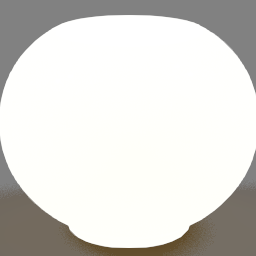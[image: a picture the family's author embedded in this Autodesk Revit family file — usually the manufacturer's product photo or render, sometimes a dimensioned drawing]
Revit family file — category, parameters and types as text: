
# Revit family: 3-020X-xx Avior Mirror
name_source: partatom
category: Lighting Fixtures
units: mm (PartAtom-declared; Revit-internal decimal feet)

## family parameters
Always vertical = Yes
Cut with Voids When Loaded = No
Host = Wall
Light Source = No
OmniClass Number = 23.80.70.00
OmniClass Title = Lighting
Part Type = Normal
Room Calculation Point = No
Round Connector Dimension = Use Diameter
Shared = No

## types (3) — shared parameters
Lamp = LED Array
Manufacturer = Vanita by Oxygen
Metal Finish 1 = 15 - Black
Model = 3-020X-xx / Avior Round
References = Ref. 3 = 120 V / Ref. 37 = 277 V
URL = www.oxygenlighting.com
Voltage = 120 V
Voltage Input = 120 V or 277 V - 50/60 Hz
zero-valued in all types: Default Elevation

## per-type parameters (varying)
| type | Diameter | Wattage Comments |
| 3-0201-15 / Black | 762 mm  [stored 2.5 ft] | 1 x 48 W at 120 V |
| 3-0202-15 / Black | 914 mm  [stored 2.99869 ft] | 1 x 50.7 W at 120 V |
| 3-0203-15 / Black | 1219 mm | 1 x 99.8 W at 120 V |

note: [stored X ft] marks values corroborated as IEEE doubles in the binary element streams (Revit-internal decimal feet)

## geometry (parser evidence)
native form markers: Sweep x5
no freeform markers — native parametric forms only
